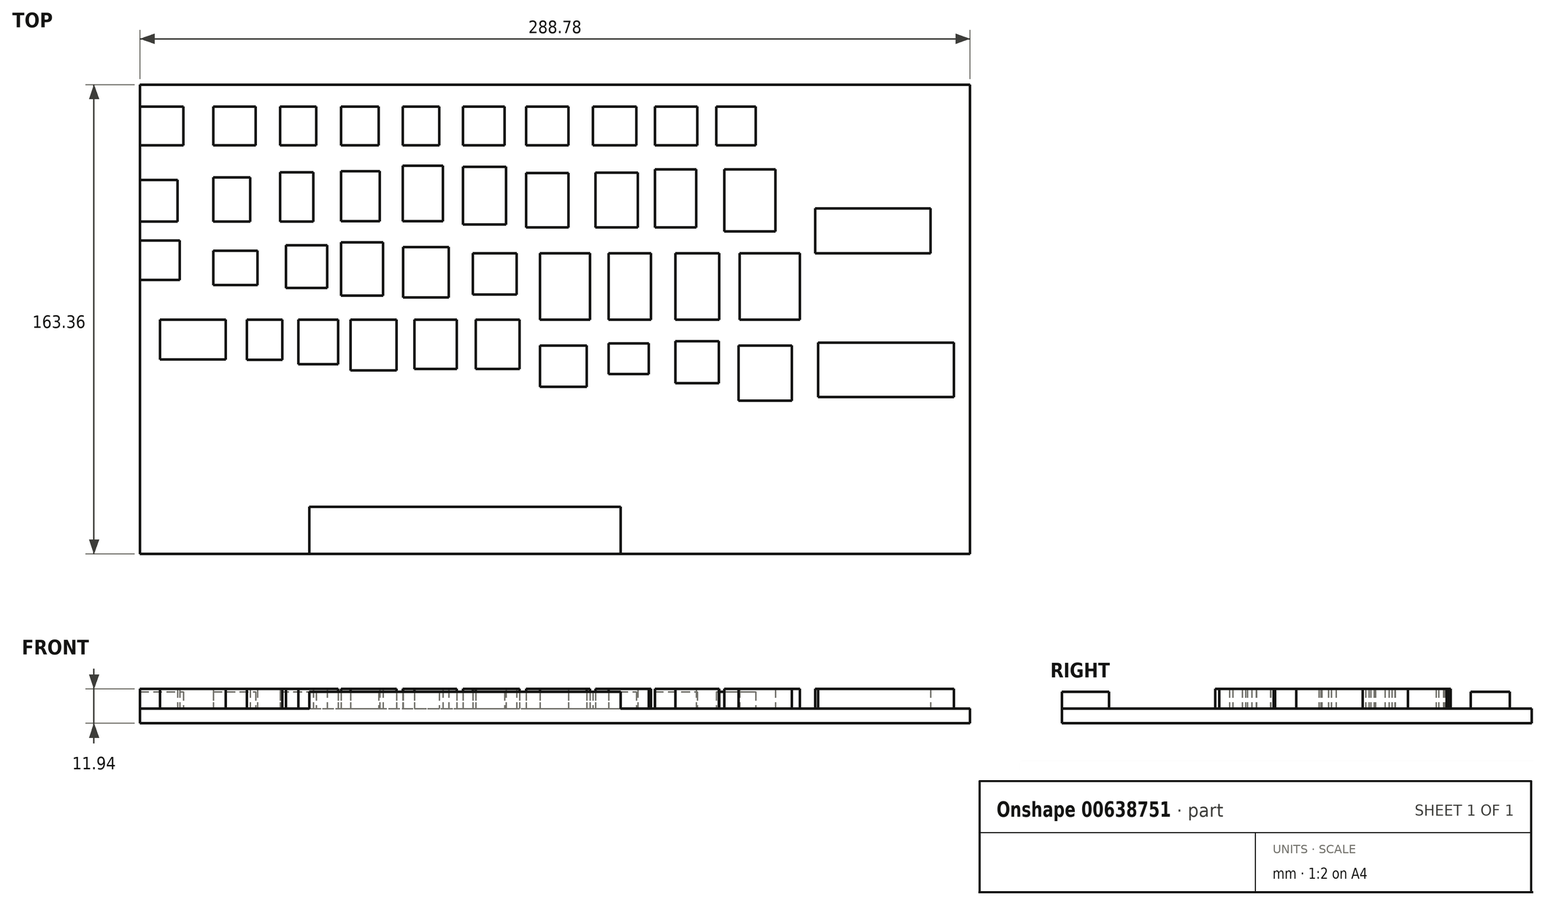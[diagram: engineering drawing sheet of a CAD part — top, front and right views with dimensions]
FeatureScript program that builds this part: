
annotation { "Feature Type Name" : "Feature", "Feature Type Description" : "" }
export const myFeature = defineFeature(function(context is Context, id is Id, definition is map)
    precondition{}
    {
        {
            var Q0;
            Q0=qCreatedBy(makeId("Top.planeOp"),FACE);
            var sketch = newSketch(context, id + "F0", { "sketchPlane" : qUnion([Q0])});
            skLineSegment(sketch, "E0.bottom", {"start": v(-149.1, 81.84) * mm, "end": v(139.68, 81.84) * mm});
            skLineSegment(sketch, "E0.top", {"start": v(-149.1, -81.52) * mm, "end": v(139.68, -81.52) * mm});
            skLineSegment(sketch, "E0.left", {"start": v(-149.1, 81.84) * mm, "end": v(-149.1, -81.52) * mm});
            skLineSegment(sketch, "E0.right", {"start": v(139.68, 81.84) * mm, "end": v(139.68, -81.52) * mm});
            skSolve(sketch);
        }
        {
            var Q0;
            Q0 = qSketchRegion(id + "F0", true);
            extrude(context, id + "F1", {"entities" : qUnion([Q0]), "depth" : 5.08 * mm, "offsetDistance" : 25.4 * mm});
        }
        {
            var Q0;
            Q0=makeQuery(id+"F1.opExtrude","CAP_FACE",FACE,{"disambiguationData":[OSD([sQuery(id+"F0.wireOp",EDGE,"E0.bottom"),sQuery(id+"F0.wireOp",EDGE,"E0.top"),sQuery(id+"F0.wireOp",EDGE,"E0.left"),sQuery(id+"F0.wireOp",EDGE,"E0.right")])],"isStart":false});
            var sketch = newSketch(context, id + "F2", { "sketchPlane" : qUnion([Q0])});
            skLineSegment(sketch, "E1.bottom", {"start": v(-149.1, 74.22) * mm, "end": v(-134.04, 74.22) * mm});
            skLineSegment(sketch, "E1.top", {"start": v(-149.1, 60.75) * mm, "end": v(-134.04, 60.75) * mm});
            skLineSegment(sketch, "E1.left", {"start": v(-149.1, 74.22) * mm, "end": v(-149.1, 60.75) * mm});
            skLineSegment(sketch, "E1.right", {"start": v(-134.04, 74.22) * mm, "end": v(-134.04, 60.75) * mm});
            skLineSegment(sketch, "E2.bottom", {"start": v(-123.62, 74.22) * mm, "end": v(-108.93, 74.22) * mm});
            skLineSegment(sketch, "E2.top", {"start": v(-123.62, 60.75) * mm, "end": v(-108.93, 60.75) * mm});
            skLineSegment(sketch, "E2.left", {"start": v(-123.62, 74.22) * mm, "end": v(-123.62, 60.75) * mm});
            skLineSegment(sketch, "E2.right", {"start": v(-108.93, 74.22) * mm, "end": v(-108.93, 60.75) * mm});
            skLineSegment(sketch, "E3.bottom", {"start": v(-100.38, 74.22) * mm, "end": v(-87.76, 74.22) * mm});
            skLineSegment(sketch, "E3.top", {"start": v(-100.38, 60.75) * mm, "end": v(-87.76, 60.75) * mm});
            skLineSegment(sketch, "E3.left", {"start": v(-100.38, 74.22) * mm, "end": v(-100.38, 60.75) * mm});
            skLineSegment(sketch, "E3.right", {"start": v(-87.76, 74.22) * mm, "end": v(-87.76, 60.75) * mm});
            skLineSegment(sketch, "E4.bottom", {"start": v(-79.24, 74.22) * mm, "end": v(-66.05, 74.22) * mm});
            skLineSegment(sketch, "E4.top", {"start": v(-79.24, 60.75) * mm, "end": v(-66.05, 60.75) * mm});
            skLineSegment(sketch, "E4.left", {"start": v(-79.24, 74.22) * mm, "end": v(-79.24, 60.75) * mm});
            skLineSegment(sketch, "E4.right", {"start": v(-66.05, 74.22) * mm, "end": v(-66.05, 60.75) * mm});
            skLineSegment(sketch, "E5.bottom", {"start": v(-57.72, 74.22) * mm, "end": v(-44.97, 74.22) * mm});
            skLineSegment(sketch, "E5.top", {"start": v(-57.72, 60.75) * mm, "end": v(-44.97, 60.75) * mm});
            skLineSegment(sketch, "E5.left", {"start": v(-57.72, 74.22) * mm, "end": v(-57.72, 60.75) * mm});
            skLineSegment(sketch, "E5.right", {"start": v(-44.97, 74.22) * mm, "end": v(-44.97, 60.75) * mm});
            skLineSegment(sketch, "E6.bottom", {"start": v(-36.71, 74.22) * mm, "end": v(-22.32, 74.22) * mm});
            skLineSegment(sketch, "E6.top", {"start": v(-36.71, 60.75) * mm, "end": v(-22.32, 60.75) * mm});
            skLineSegment(sketch, "E6.left", {"start": v(-36.71, 74.22) * mm, "end": v(-36.71, 60.75) * mm});
            skLineSegment(sketch, "E6.right", {"start": v(-22.32, 74.22) * mm, "end": v(-22.32, 60.75) * mm});
            skLineSegment(sketch, "E7.bottom", {"start": v(-14.84, 74.22) * mm, "end": v(0, 74.22) * mm});
            skLineSegment(sketch, "E7.top", {"start": v(-14.84, 60.75) * mm, "end": v(0, 60.75) * mm});
            skLineSegment(sketch, "E7.left", {"start": v(-14.84, 74.22) * mm, "end": v(-14.84, 60.75) * mm});
            skLineSegment(sketch, "E7.right", {"start": v(0, 74.22) * mm, "end": v(0, 60.75) * mm});
            skLineSegment(sketch, "E8.bottom", {"start": v(8.47, 74.22) * mm, "end": v(23.53, 74.22) * mm});
            skLineSegment(sketch, "E8.top", {"start": v(8.47, 60.75) * mm, "end": v(23.53, 60.75) * mm});
            skLineSegment(sketch, "E8.left", {"start": v(8.47, 74.22) * mm, "end": v(8.47, 60.75) * mm});
            skLineSegment(sketch, "E8.right", {"start": v(23.53, 74.22) * mm, "end": v(23.53, 60.75) * mm});
            skLineSegment(sketch, "E9.bottom", {"start": v(29.98, 74.22) * mm, "end": v(44.8, 74.22) * mm});
            skLineSegment(sketch, "E9.top", {"start": v(29.98, 60.75) * mm, "end": v(44.8, 60.75) * mm});
            skLineSegment(sketch, "E9.left", {"start": v(29.98, 74.22) * mm, "end": v(29.98, 60.75) * mm});
            skLineSegment(sketch, "E9.right", {"start": v(44.8, 74.22) * mm, "end": v(44.8, 60.75) * mm});
            skLineSegment(sketch, "E10.bottom", {"start": v(51.43, 74.22) * mm, "end": v(65.12, 74.22) * mm});
            skLineSegment(sketch, "E10.top", {"start": v(51.43, 60.75) * mm, "end": v(65.12, 60.75) * mm});
            skLineSegment(sketch, "E10.left", {"start": v(51.43, 74.22) * mm, "end": v(51.43, 60.75) * mm});
            skLineSegment(sketch, "E10.right", {"start": v(65.12, 74.22) * mm, "end": v(65.12, 60.75) * mm});
            skSolve(sketch);
        }
        {
            var Q0;
            Q0 = qSketchRegion(id + "F2", true);
            extrude(context, id + "F3", {"entities" : qUnion([Q0]), "operationType" : NewBodyOperationType.ADD, "depth" : 5.84 * mm, "offsetDistance" : 25.4 * mm});
        }
        {
            var Q0;
            Q0=makeQuery(id+"F1.opExtrude","CAP_FACE",FACE,{"disambiguationData":[OSD([sQuery(id+"F0.wireOp",EDGE,"E0.bottom"),sQuery(id+"F0.wireOp",EDGE,"E0.top"),sQuery(id+"F0.wireOp",EDGE,"E0.left"),sQuery(id+"F0.wireOp",EDGE,"E0.right")])],"isStart":false});
            var sketch = newSketch(context, id + "F4", { "sketchPlane" : qUnion([Q0])});
            skLineSegment(sketch, "E11.bottom", {"start": v(-90.21, -65.14) * mm, "end": v(18.08, -65.14) * mm});
            skLineSegment(sketch, "E11.top", {"start": v(-90.21, -81.52) * mm, "end": v(18.08, -81.52) * mm});
            skLineSegment(sketch, "E11.left", {"start": v(-90.21, -65.14) * mm, "end": v(-90.21, -81.52) * mm});
            skLineSegment(sketch, "E11.right", {"start": v(18.08, -65.14) * mm, "end": v(18.08, -81.52) * mm});
            skSolve(sketch);
        }
        {
            var Q0;
            Q0 = qSketchRegion(id + "F4", true);
            extrude(context, id + "F5", {"entities" : qUnion([Q0]), "operationType" : NewBodyOperationType.ADD, "depth" : 5.84 * mm, "offsetDistance" : 25.4 * mm});
        }
        {
            var Q0;
            Q0=makeQuery(id+"F1.opExtrude","CAP_FACE",FACE,{"disambiguationData":[OSD([sQuery(id+"F0.wireOp",EDGE,"E0.bottom"),sQuery(id+"F0.wireOp",EDGE,"E0.top"),sQuery(id+"F0.wireOp",EDGE,"E0.left"),sQuery(id+"F0.wireOp",EDGE,"E0.right")])],"isStart":false});
            var sketch = newSketch(context, id + "F6", { "sketchPlane" : qUnion([Q0])});
            skLineSegment(sketch, "E12.bottom", {"start": v(-149.1, 48.66) * mm, "end": v(-136.03, 48.66) * mm});
            skLineSegment(sketch, "E12.top", {"start": v(-149.1, 34.21) * mm, "end": v(-136.03, 34.21) * mm});
            skLineSegment(sketch, "E12.left", {"start": v(-149.1, 48.66) * mm, "end": v(-149.1, 34.21) * mm});
            skLineSegment(sketch, "E12.right", {"start": v(-136.03, 48.66) * mm, "end": v(-136.03, 34.21) * mm});
            skLineSegment(sketch, "E13.bottom", {"start": v(-123.62, 49.52) * mm, "end": v(-110.83, 49.52) * mm});
            skLineSegment(sketch, "E13.top", {"start": v(-123.62, 34.21) * mm, "end": v(-110.83, 34.21) * mm});
            skLineSegment(sketch, "E13.left", {"start": v(-123.62, 49.52) * mm, "end": v(-123.62, 34.21) * mm});
            skLineSegment(sketch, "E13.right", {"start": v(-110.83, 49.52) * mm, "end": v(-110.83, 34.21) * mm});
            skLineSegment(sketch, "E14.bottom", {"start": v(-100.34, 51.35) * mm, "end": v(-88.88, 51.35) * mm});
            skLineSegment(sketch, "E14.top", {"start": v(-100.34, 34.21) * mm, "end": v(-88.88, 34.21) * mm});
            skLineSegment(sketch, "E14.left", {"start": v(-100.34, 51.35) * mm, "end": v(-100.34, 34.21) * mm});
            skLineSegment(sketch, "E14.right", {"start": v(-88.88, 51.35) * mm, "end": v(-88.88, 34.21) * mm});
            skLineSegment(sketch, "E15.bottom", {"start": v(-79.24, 51.7) * mm, "end": v(-65.74, 51.7) * mm});
            skLineSegment(sketch, "E15.top", {"start": v(-79.24, 34.4) * mm, "end": v(-65.74, 34.4) * mm});
            skLineSegment(sketch, "E15.left", {"start": v(-79.24, 51.7) * mm, "end": v(-79.24, 34.4) * mm});
            skLineSegment(sketch, "E15.right", {"start": v(-65.74, 51.7) * mm, "end": v(-65.74, 34.4) * mm});
            skLineSegment(sketch, "E16.bottom", {"start": v(-57.72, 53.65) * mm, "end": v(-43.8, 53.65) * mm});
            skLineSegment(sketch, "E16.top", {"start": v(-57.72, 34.37) * mm, "end": v(-43.8, 34.37) * mm});
            skLineSegment(sketch, "E16.left", {"start": v(-57.72, 53.65) * mm, "end": v(-57.72, 34.37) * mm});
            skLineSegment(sketch, "E16.right", {"start": v(-43.8, 53.65) * mm, "end": v(-43.8, 34.37) * mm});
            skLineSegment(sketch, "E17.bottom", {"start": v(-36.71, 53.26) * mm, "end": v(-21.78, 53.26) * mm});
            skLineSegment(sketch, "E17.top", {"start": v(-36.71, 33.23) * mm, "end": v(-21.78, 33.23) * mm});
            skLineSegment(sketch, "E17.left", {"start": v(-36.71, 53.26) * mm, "end": v(-36.71, 33.23) * mm});
            skLineSegment(sketch, "E17.right", {"start": v(-21.78, 53.26) * mm, "end": v(-21.78, 33.23) * mm});
            skLineSegment(sketch, "E18.bottom", {"start": v(-14.84, 51.12) * mm, "end": v(0, 51.12) * mm});
            skLineSegment(sketch, "E18.top", {"start": v(-14.84, 32.22) * mm, "end": v(0, 32.22) * mm});
            skLineSegment(sketch, "E18.left", {"start": v(-14.84, 51.12) * mm, "end": v(-14.84, 32.22) * mm});
            skLineSegment(sketch, "E18.right", {"start": v(0, 51.12) * mm, "end": v(0, 32.22) * mm});
            skLineSegment(sketch, "E19.bottom", {"start": v(9.38, 51.22) * mm, "end": v(24.07, 51.22) * mm});
            skLineSegment(sketch, "E19.top", {"start": v(9.38, 32.22) * mm, "end": v(24.07, 32.22) * mm});
            skLineSegment(sketch, "E19.left", {"start": v(9.38, 51.22) * mm, "end": v(9.38, 32.22) * mm});
            skLineSegment(sketch, "E19.right", {"start": v(24.07, 51.22) * mm, "end": v(24.07, 32.22) * mm});
            skLineSegment(sketch, "E20.bottom", {"start": v(29.98, 52.31) * mm, "end": v(44.35, 52.31) * mm});
            skLineSegment(sketch, "E20.top", {"start": v(29.98, 32.22) * mm, "end": v(44.35, 32.22) * mm});
            skLineSegment(sketch, "E20.left", {"start": v(29.98, 52.31) * mm, "end": v(29.98, 32.22) * mm});
            skLineSegment(sketch, "E20.right", {"start": v(44.35, 52.31) * mm, "end": v(44.35, 32.22) * mm});
            skLineSegment(sketch, "E21.bottom", {"start": v(54.2, 52.31) * mm, "end": v(71.95, 52.31) * mm});
            skLineSegment(sketch, "E21.top", {"start": v(54.2, 30.8) * mm, "end": v(71.95, 30.8) * mm});
            skLineSegment(sketch, "E21.left", {"start": v(54.2, 52.31) * mm, "end": v(54.2, 30.8) * mm});
            skLineSegment(sketch, "E21.right", {"start": v(71.95, 52.31) * mm, "end": v(71.95, 30.8) * mm});
            skLineSegment(sketch, "E22.bottom", {"start": v(-149.1, 27.6) * mm, "end": v(-135.26, 27.6) * mm});
            skLineSegment(sketch, "E22.top", {"start": v(-149.1, 13.88) * mm, "end": v(-135.26, 13.88) * mm});
            skLineSegment(sketch, "E22.left", {"start": v(-149.1, 27.6) * mm, "end": v(-149.1, 13.88) * mm});
            skLineSegment(sketch, "E22.right", {"start": v(-135.26, 27.6) * mm, "end": v(-135.26, 13.88) * mm});
            skLineSegment(sketch, "E23.bottom", {"start": v(-123.62, 24.1) * mm, "end": v(-108.29, 24.1) * mm});
            skLineSegment(sketch, "E23.top", {"start": v(-123.62, 12.14) * mm, "end": v(-108.29, 12.14) * mm});
            skLineSegment(sketch, "E23.left", {"start": v(-123.62, 24.1) * mm, "end": v(-123.62, 12.14) * mm});
            skLineSegment(sketch, "E23.right", {"start": v(-108.29, 24.1) * mm, "end": v(-108.29, 12.14) * mm});
            skLineSegment(sketch, "E24.bottom", {"start": v(-98.37, 25.95) * mm, "end": v(-84.04, 25.95) * mm});
            skLineSegment(sketch, "E24.top", {"start": v(-98.37, 11.14) * mm, "end": v(-84.04, 11.14) * mm});
            skLineSegment(sketch, "E24.left", {"start": v(-98.37, 25.95) * mm, "end": v(-98.37, 11.14) * mm});
            skLineSegment(sketch, "E24.right", {"start": v(-84.04, 25.95) * mm, "end": v(-84.04, 11.14) * mm});
            skLineSegment(sketch, "E25.bottom", {"start": v(-79.24, 27.02) * mm, "end": v(-64.63, 27.02) * mm});
            skLineSegment(sketch, "E25.top", {"start": v(-79.24, 8.5) * mm, "end": v(-64.63, 8.5) * mm});
            skLineSegment(sketch, "E25.left", {"start": v(-79.24, 27.02) * mm, "end": v(-79.24, 8.5) * mm});
            skLineSegment(sketch, "E25.right", {"start": v(-64.63, 27.02) * mm, "end": v(-64.63, 8.5) * mm});
            skLineSegment(sketch, "E26.bottom", {"start": v(-57.58, 25.26) * mm, "end": v(-41.75, 25.26) * mm});
            skLineSegment(sketch, "E26.top", {"start": v(-57.58, 7.85) * mm, "end": v(-41.75, 7.85) * mm});
            skLineSegment(sketch, "E26.left", {"start": v(-57.58, 25.26) * mm, "end": v(-57.58, 7.85) * mm});
            skLineSegment(sketch, "E26.right", {"start": v(-41.75, 25.26) * mm, "end": v(-41.75, 7.85) * mm});
            skLineSegment(sketch, "E27.bottom", {"start": v(-33.27, 23.14) * mm, "end": v(-18.08, 23.14) * mm});
            skLineSegment(sketch, "E27.top", {"start": v(-33.27, 8.83) * mm, "end": v(-18.08, 8.83) * mm});
            skLineSegment(sketch, "E27.left", {"start": v(-33.27, 23.14) * mm, "end": v(-33.27, 8.83) * mm});
            skLineSegment(sketch, "E27.right", {"start": v(-18.08, 23.14) * mm, "end": v(-18.08, 8.83) * mm});
            skPoint(sketch, "E28.firstSnap0", {"position": v(-142.18, 13.88) * mm});
            skLineSegment(sketch, "E28.bottom", {"start": v(-142.18, 0) * mm, "end": v(-119.27, 0) * mm});
            skLineSegment(sketch, "E28.top", {"start": v(-142.18, -13.82) * mm, "end": v(-119.27, -13.82) * mm});
            skLineSegment(sketch, "E28.left", {"start": v(-142.18, 0) * mm, "end": v(-142.18, -13.82) * mm});
            skLineSegment(sketch, "E28.right", {"start": v(-119.27, 0) * mm, "end": v(-119.27, -13.82) * mm});
            skLineSegment(sketch, "E29.bottom", {"start": v(-9.9, 23.14) * mm, "end": v(0, 23.14) * mm});
            skLineSegment(sketch, "E29.top", {"start": v(-9.9, 6.82) * mm, "end": v(0, 6.82) * mm});
            skLineSegment(sketch, "E29.left", {"start": v(-9.9, 23.14) * mm, "end": v(-9.9, 6.82) * mm});
            skLineSegment(sketch, "E29.right", {"start": v(0, 23.14) * mm, "end": v(0, 6.82) * mm});
            skLineSegment(sketch, "E30.bottom", {"start": v(13.92, 23.14) * mm, "end": v(28.67, 23.14) * mm});
            skLineSegment(sketch, "E30.top", {"start": v(13.92, 0) * mm, "end": v(28.67, 0) * mm});
            skLineSegment(sketch, "E30.left", {"start": v(13.92, 23.14) * mm, "end": v(13.92, 0) * mm});
            skLineSegment(sketch, "E30.right", {"start": v(28.67, 23.14) * mm, "end": v(28.67, 0) * mm});
            skPoint(sketch, "E31.firstSnap0", {"position": v(37.16, 32.22) * mm});
            skLineSegment(sketch, "E31.bottom", {"start": v(37.16, 23.14) * mm, "end": v(52.38, 23.14) * mm});
            skLineSegment(sketch, "E31.top", {"start": v(37.16, 0) * mm, "end": v(52.38, 0) * mm});
            skLineSegment(sketch, "E31.left", {"start": v(37.16, 23.14) * mm, "end": v(37.16, 0) * mm});
            skLineSegment(sketch, "E31.right", {"start": v(52.38, 23.14) * mm, "end": v(52.38, 0) * mm});
            skLineSegment(sketch, "E32.bottom", {"start": v(59.47, 23.14) * mm, "end": v(80.52, 23.14) * mm});
            skLineSegment(sketch, "E32.top", {"start": v(59.47, 0) * mm, "end": v(80.52, 0) * mm});
            skLineSegment(sketch, "E32.left", {"start": v(59.47, 23.14) * mm, "end": v(59.47, 0) * mm});
            skLineSegment(sketch, "E32.right", {"start": v(80.52, 23.14) * mm, "end": v(80.52, 0) * mm});
            skLineSegment(sketch, "E33.bottom", {"start": v(85.8, 38.8) * mm, "end": v(125.87, 38.8) * mm});
            skLineSegment(sketch, "E33.top", {"start": v(85.8, 23.14) * mm, "end": v(125.87, 23.14) * mm});
            skLineSegment(sketch, "E33.left", {"start": v(85.8, 38.8) * mm, "end": v(85.8, 23.14) * mm});
            skLineSegment(sketch, "E33.right", {"start": v(125.87, 38.8) * mm, "end": v(125.87, 23.14) * mm});
            skLineSegment(sketch, "E34.bottom", {"start": v(86.82, -7.94) * mm, "end": v(134.07, -7.94) * mm});
            skLineSegment(sketch, "E34.top", {"start": v(86.82, -26.82) * mm, "end": v(134.07, -26.82) * mm});
            skLineSegment(sketch, "E34.left", {"start": v(86.82, -7.94) * mm, "end": v(86.82, -26.82) * mm});
            skLineSegment(sketch, "E34.right", {"start": v(134.07, -7.94) * mm, "end": v(134.07, -26.82) * mm});
            skLineSegment(sketch, "E35.bottom", {"start": v(-111.94, 0) * mm, "end": v(-99.55, 0) * mm});
            skLineSegment(sketch, "E35.top", {"start": v(-111.94, -13.98) * mm, "end": v(-99.55, -13.98) * mm});
            skLineSegment(sketch, "E35.left", {"start": v(-111.94, 0) * mm, "end": v(-111.94, -13.98) * mm});
            skLineSegment(sketch, "E35.right", {"start": v(-99.55, 0) * mm, "end": v(-99.55, -13.98) * mm});
            skLineSegment(sketch, "E36.bottom", {"start": v(-94.1, 0) * mm, "end": v(-80.2, 0) * mm});
            skLineSegment(sketch, "E36.top", {"start": v(-94.1, -15.5) * mm, "end": v(-80.2, -15.5) * mm});
            skLineSegment(sketch, "E36.left", {"start": v(-94.1, 0) * mm, "end": v(-94.1, -15.5) * mm});
            skLineSegment(sketch, "E36.right", {"start": v(-80.2, 0) * mm, "end": v(-80.2, -15.5) * mm});
            skLineSegment(sketch, "E37.bottom", {"start": v(-75.82, 0) * mm, "end": v(-59.93, 0) * mm});
            skLineSegment(sketch, "E37.top", {"start": v(-75.82, -17.64) * mm, "end": v(-59.93, -17.64) * mm});
            skLineSegment(sketch, "E37.left", {"start": v(-75.82, 0) * mm, "end": v(-75.82, -17.64) * mm});
            skLineSegment(sketch, "E37.right", {"start": v(-59.93, 0) * mm, "end": v(-59.93, -17.64) * mm});
            skLineSegment(sketch, "E38.bottom", {"start": v(-53.67, 0) * mm, "end": v(-38.92, 0) * mm});
            skLineSegment(sketch, "E38.top", {"start": v(-53.67, -17.05) * mm, "end": v(-38.92, -17.05) * mm});
            skLineSegment(sketch, "E38.left", {"start": v(-53.67, 0) * mm, "end": v(-53.67, -17.05) * mm});
            skLineSegment(sketch, "E38.right", {"start": v(-38.92, 0) * mm, "end": v(-38.92, -17.05) * mm});
            skLineSegment(sketch, "E39.bottom", {"start": v(-9.9, 23.14) * mm, "end": v(7.5, 23.14) * mm});
            skLineSegment(sketch, "E39.top", {"start": v(-9.9, 0) * mm, "end": v(7.5, 0) * mm});
            skLineSegment(sketch, "E39.left", {"start": v(-9.9, 23.14) * mm, "end": v(-9.9, 0) * mm});
            skLineSegment(sketch, "E39.right", {"start": v(7.5, 23.14) * mm, "end": v(7.5, 0) * mm});
            skLineSegment(sketch, "E40.bottom", {"start": v(-32.36, 0) * mm, "end": v(-17.1, 0) * mm});
            skLineSegment(sketch, "E40.top", {"start": v(-32.36, -17.05) * mm, "end": v(-17.1, -17.05) * mm});
            skLineSegment(sketch, "E40.left", {"start": v(-32.36, 0) * mm, "end": v(-32.36, -17.05) * mm});
            skLineSegment(sketch, "E40.right", {"start": v(-17.1, 0) * mm, "end": v(-17.1, -17.05) * mm});
            skLineSegment(sketch, "E41.bottom", {"start": v(-9.9, -8.99) * mm, "end": v(6.24, -8.99) * mm});
            skLineSegment(sketch, "E41.top", {"start": v(-9.9, -23.3) * mm, "end": v(6.24, -23.3) * mm});
            skLineSegment(sketch, "E41.left", {"start": v(-9.9, -8.99) * mm, "end": v(-9.9, -23.3) * mm});
            skLineSegment(sketch, "E41.right", {"start": v(6.24, -8.99) * mm, "end": v(6.24, -23.3) * mm});
            skLineSegment(sketch, "E42.bottom", {"start": v(13.92, -8.15) * mm, "end": v(27.91, -8.15) * mm});
            skLineSegment(sketch, "E42.top", {"start": v(13.92, -18.86) * mm, "end": v(27.91, -18.86) * mm});
            skLineSegment(sketch, "E42.left", {"start": v(13.92, -8.15) * mm, "end": v(13.92, -18.86) * mm});
            skLineSegment(sketch, "E42.right", {"start": v(27.91, -8.15) * mm, "end": v(27.91, -18.86) * mm});
            skLineSegment(sketch, "E43.bottom", {"start": v(37.16, -7.42) * mm, "end": v(52.29, -7.42) * mm});
            skLineSegment(sketch, "E43.top", {"start": v(37.16, -22.1) * mm, "end": v(52.29, -22.1) * mm});
            skLineSegment(sketch, "E43.left", {"start": v(37.16, -7.42) * mm, "end": v(37.16, -22.1) * mm});
            skLineSegment(sketch, "E43.right", {"start": v(52.29, -7.42) * mm, "end": v(52.29, -22.1) * mm});
            skLineSegment(sketch, "E44.bottom", {"start": v(59.11, -8.93) * mm, "end": v(77.73, -8.93) * mm});
            skLineSegment(sketch, "E44.top", {"start": v(59.11, -28.19) * mm, "end": v(77.73, -28.19) * mm});
            skLineSegment(sketch, "E44.left", {"start": v(59.11, -8.93) * mm, "end": v(59.11, -28.19) * mm});
            skLineSegment(sketch, "E44.right", {"start": v(77.73, -8.93) * mm, "end": v(77.73, -28.19) * mm});
            skSolve(sketch);
        }
        {
            var Q0;
            Q0 = qSketchRegion(id + "F6", true);
            extrude(context, id + "F7", {"entities" : qUnion([Q0]), "operationType" : NewBodyOperationType.ADD, "depth" : 6.86 * mm, "offsetDistance" : 25.4 * mm});
        }
    });
